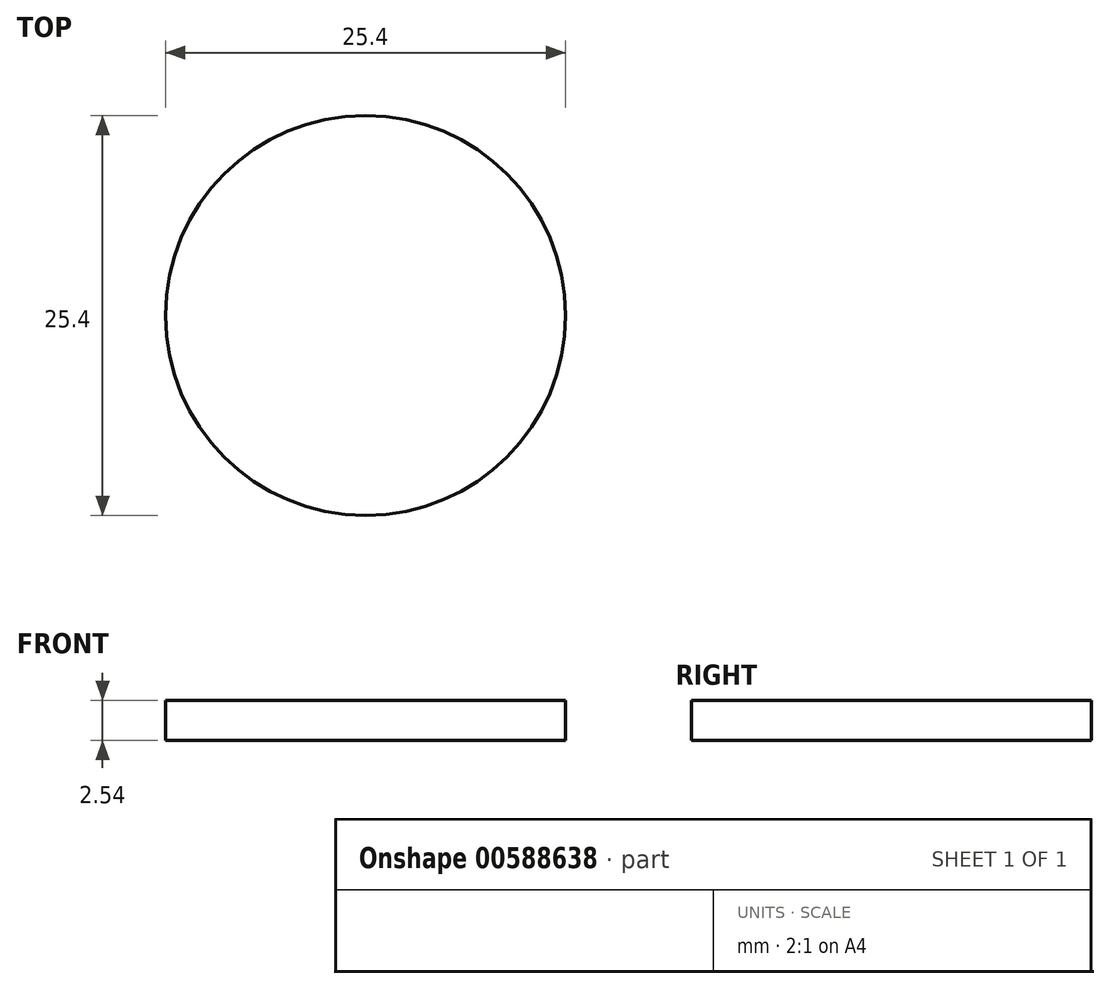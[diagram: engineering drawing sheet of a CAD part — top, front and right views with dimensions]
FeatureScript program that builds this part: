
annotation { "Feature Type Name" : "Feature", "Feature Type Description" : "" }
export const myFeature = defineFeature(function(context is Context, id is Id, definition is map)
    precondition{}
    {
        {
            var Q0;
            Q0=qCreatedBy(makeId("Top.planeOp"),FACE);
            var sketch = newSketch(context, id + "F0", { "sketchPlane" : qUnion([Q0])});
            skCircle(sketch, "E0", {"center": v(0, 0) * mm, "radius": 12.7 * mm});
            skSolve(sketch);
        }
        {
            var Q0;
            Q0 = qSketchRegion(id + "F0", true);
            extrude(context, id + "F1", {"entities" : qUnion([Q0]), "depth" : 2.54 * mm, "offsetDistance" : 25 * mm});
        }
    });
